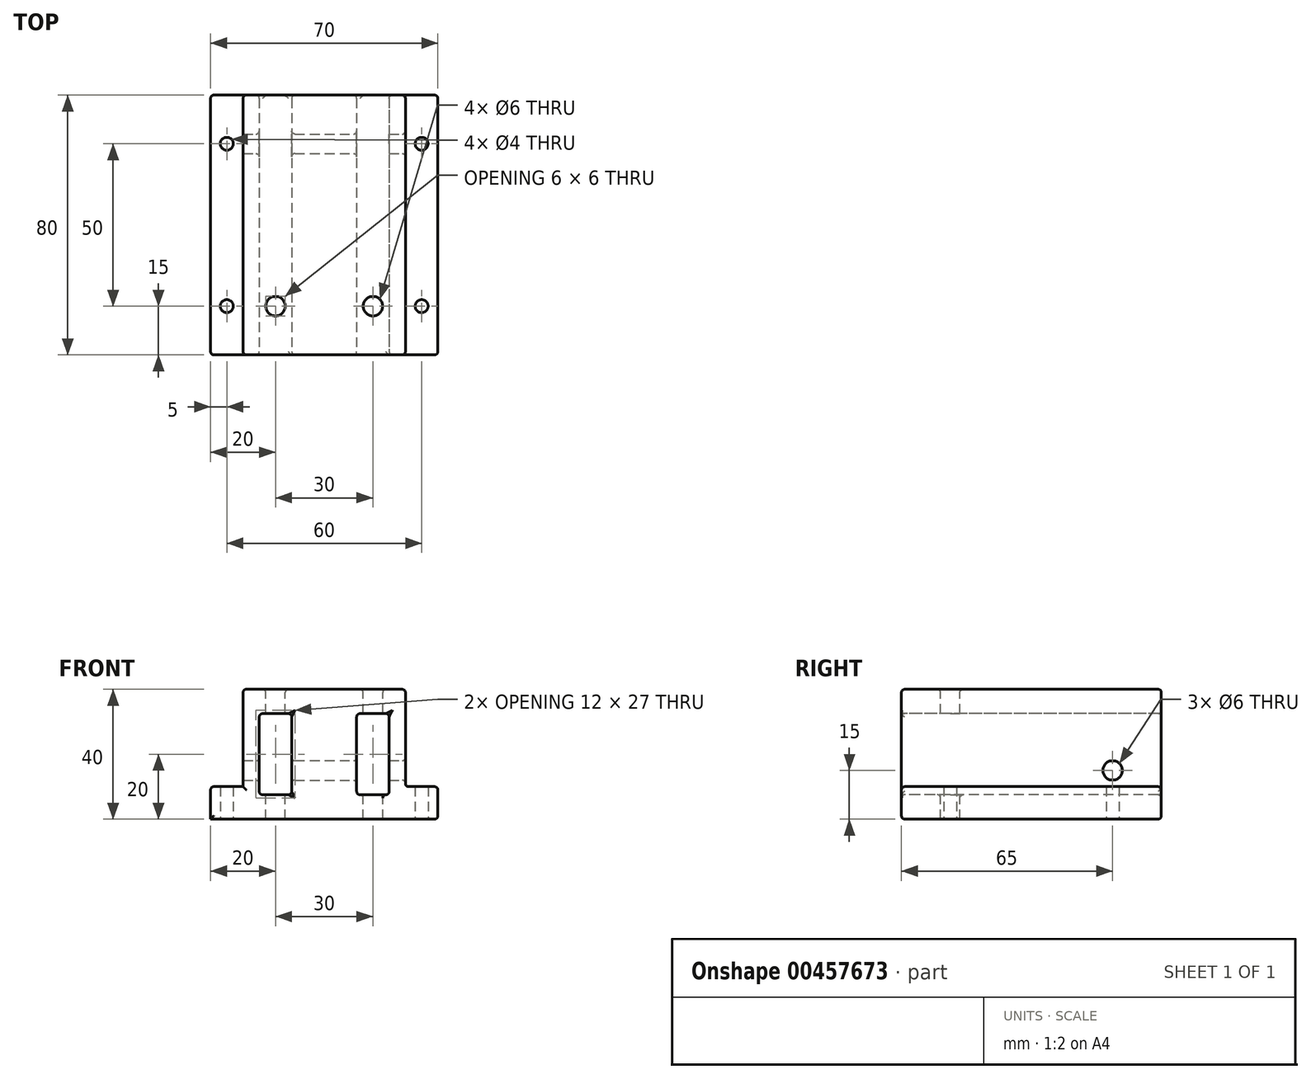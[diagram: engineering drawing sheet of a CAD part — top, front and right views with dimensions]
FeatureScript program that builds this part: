
annotation { "Feature Type Name" : "Feature", "Feature Type Description" : "" }
export const myFeature = defineFeature(function(context is Context, id is Id, definition is map)
    precondition{}
    {
        {
            var Q0;
            Q0=qCreatedBy(makeId("Front.planeOp"),FACE);
            var sketch = newSketch(context, id + "F0", { "sketchPlane" : qUnion([Q0])});
            skLineSegment(sketch, "E0.bottom", {"start": v(-25, 20) * mm, "end": v(25, 20) * mm});
            skLineSegment(sketch, "E0.top", {"start": v(-25, -20) * mm, "end": v(25, -20) * mm});
            skLineSegment(sketch, "E0.left", {"start": v(-25, 20) * mm, "end": v(-25, -20) * mm});
            skLineSegment(sketch, "E0.right", {"start": v(25, 20) * mm, "end": v(25, -20) * mm});
            skPoint(sketch, "E0.middle", {"position": v(0, 0) * mm});
            skSolve(sketch);
        }
        {
            var Q0;
            Q0 = qSketchRegion(id + "F0", true);
            extrude(context, id + "F1", {"entities" : qUnion([Q0]), "depth" : 80 * mm});
        }
        {
            var Q0;
            Q0=makeQuery(id+"F1.opExtrude","CAP_FACE",FACE,{"disambiguationData":[OSD([sQuery(id+"F0.wireOp",EDGE,"E0.bottom"),sQuery(id+"F0.wireOp",EDGE,"E0.top"),sQuery(id+"F0.wireOp",EDGE,"E0.left"),sQuery(id+"F0.wireOp",EDGE,"E0.right")])],"isStart":false});
            var sketch = newSketch(context, id + "F2", { "sketchPlane" : qUnion([Q0])});
            skPoint(sketch, "E1", {"position": v(-15, 0) * mm});
            skPoint(sketch, "E2", {"position": v(15, 0) * mm});
            skLineSegment(sketch, "E3.bottom", {"start": v(-20, 12.5) * mm, "end": v(-10, 12.5) * mm});
            skLineSegment(sketch, "E3.top", {"start": v(-20, -12.5) * mm, "end": v(-10, -12.5) * mm});
            skLineSegment(sketch, "E3.left", {"start": v(-20, 12.5) * mm, "end": v(-20, -12.5) * mm});
            skLineSegment(sketch, "E3.right", {"start": v(-10, 12.5) * mm, "end": v(-10, -12.5) * mm});
            skLineSegment(sketch, "E4.bottom", {"start": v(10, 12.5) * mm, "end": v(20, 12.5) * mm});
            skLineSegment(sketch, "E4.top", {"start": v(10, -12.5) * mm, "end": v(20, -12.5) * mm});
            skLineSegment(sketch, "E4.left", {"start": v(10, 12.5) * mm, "end": v(10, -12.5) * mm});
            skLineSegment(sketch, "E4.right", {"start": v(20, 12.5) * mm, "end": v(20, -12.5) * mm});
            skSolve(sketch);
        }
        {
            var Q0;
            Q0 = qSketchRegion(id + "F2", true);
            extrude(context, id + "F3", {"entities" : qUnion([Q0]), "operationType" : NewBodyOperationType.REMOVE, "endBound" : BoundingType.THROUGH_ALL, "oppositeDirection" : true, "depth" : 25 * mm});
        }
        {
            var Q0;
            Q0=makeQuery(id+"F1.opExtrude","SWEPT_FACE",FACE,{"disambiguationData":[OSD([sQuery(id+"F0.wireOp",EDGE,"E0.right")])]});
            var sketch = newSketch(context, id + "F4", { "sketchPlane" : qUnion([Q0])});
            skPoint(sketch, "E5", {"position": v(-15, -5) * mm});
            skSolve(sketch);
        }
        {
            var Q0;
            Q0=sQuery(id+"F4.wireOp",VERTEX,"E5");
            var Q1;
            Q1=makeQuery(id+"F1.opExtrude","SWEPT_BODY",BODY,{"disambiguationData":[OSD([sQuery(id+"F0.wireOp",EDGE,"E0.bottom"),sQuery(id+"F0.wireOp",EDGE,"E0.top"),sQuery(id+"F0.wireOp",EDGE,"E0.left"),sQuery(id+"F0.wireOp",EDGE,"E0.right")])]});
            hole(context, id + "F5", {"style" : HoleStyle.SIMPLE, "endStyle" : HoleEndStyle.THROUGH, "holeDiameter" : 6 * mm, "isTappedThrough" : true, "tappedDepth" : 12 * mm, "tapClearance" : 3, "startFromSketch" : true, "locations" : qUnion([Q0]), "scope" : qUnion([Q1])});
        }
        {
            var Q0;
            Q0=makeQuery(id+"F1.opExtrude","SWEPT_FACE",FACE,{"disambiguationData":[OSD([sQuery(id+"F0.wireOp",EDGE,"E0.bottom")])]});
            var sketch = newSketch(context, id + "F6", { "sketchPlane" : qUnion([Q0])});
            skPoint(sketch, "E6", {"position": v(-15, -65) * mm});
            skPoint(sketch, "E7", {"position": v(15, -65) * mm});
            skSolve(sketch);
        }
        {
            var Q0;
            Q0=sQuery(id+"F6.wireOp",VERTEX,"E6");
            var Q1;
            Q1=sQuery(id+"F6.wireOp",VERTEX,"E7");
            var Q2;
            Q2=makeQuery(id+"F1.opExtrude","SWEPT_BODY",BODY,{"disambiguationData":[OSD([sQuery(id+"F0.wireOp",EDGE,"E0.bottom"),sQuery(id+"F0.wireOp",EDGE,"E0.top"),sQuery(id+"F0.wireOp",EDGE,"E0.left"),sQuery(id+"F0.wireOp",EDGE,"E0.right")])]});
            hole(context, id + "F7", {"style" : HoleStyle.SIMPLE, "endStyle" : HoleEndStyle.THROUGH, "holeDiameter" : 6 * mm, "isTappedThrough" : true, "tappedDepth" : 12 * mm, "tapClearance" : 3, "startFromSketch" : true, "locations" : qUnion([Q0, Q1]), "scope" : qUnion([Q2])});
        }
        {
            var Q0;
            Q0=makeQuery(id+"F1.opExtrude","SWEPT_FACE",FACE,{"disambiguationData":[OSD([sQuery(id+"F0.wireOp",EDGE,"E0.right")])]});
            var sketch = newSketch(context, id + "F8", { "sketchPlane" : qUnion([Q0])});
            skLineSegment(sketch, "E8", {"start": v(-80, -10) * mm, "end": v(0, -10) * mm});
            skSolve(sketch);
        }
        {
            var Q0;
            {var subQ0=sQuery(id+"F8.wireOp",EDGE,"E8");Q0=makeQuery(id+"F8.imprint","IMPRINT",FACE,{"disambiguationData":[TD([[makeQuery(id+"F8.imprint","IMPRINT",EDGE,{"derivedFrom":subQ0}),-1.0]])]});}
            extrude(context, id + "F9", {"entities" : qUnion([Q0]), "depth" : 10 * mm});
        }
        {
            var Q0;
            Q0=makeQuery(id+"F1.opExtrude","SWEPT_FACE",FACE,{"disambiguationData":[OSD([sQuery(id+"F0.wireOp",EDGE,"E0.left")])]});
            var sketch = newSketch(context, id + "F10", { "sketchPlane" : qUnion([Q0])});
            skLineSegment(sketch, "E9", {"start": v(0, -10) * mm, "end": v(80, -10) * mm});
            skSolve(sketch);
        }
        {
            var Q0;
            {var subQ0=sQuery(id+"F10.wireOp",EDGE,"E9");Q0=makeQuery(id+"F10.imprint","IMPRINT",FACE,{"disambiguationData":[TD([[makeQuery(id+"F10.imprint","IMPRINT",EDGE,{"derivedFrom":subQ0}),-1.0]])]});}
            extrude(context, id + "F11", {"entities" : qUnion([Q0]), "depth" : 10 * mm});
        }
        {
            var Q0;
            Q0=makeQuery(id+"F11.opExtrude","SWEPT_BODY",BODY,{"disambiguationData":[OSD([sQuery(id+"F0.wireOp",EDGE,"E0.top"),sQuery(id+"F0.wireOp",EDGE,"E0.left"),sQuery(id+"F10.wireOp",EDGE,"E9")])]});
            var Q1;
            Q1=makeQuery(id+"F1.opExtrude","SWEPT_BODY",BODY,{"disambiguationData":[OSD([sQuery(id+"F0.wireOp",EDGE,"E0.bottom"),sQuery(id+"F0.wireOp",EDGE,"E0.top"),sQuery(id+"F0.wireOp",EDGE,"E0.left"),sQuery(id+"F0.wireOp",EDGE,"E0.right")])]});
            var Q2;
            Q2=makeQuery(id+"F9.opExtrude","SWEPT_BODY",BODY,{"disambiguationData":[OSD([sQuery(id+"F0.wireOp",EDGE,"E0.top"),sQuery(id+"F0.wireOp",EDGE,"E0.right"),sQuery(id+"F8.wireOp",EDGE,"E8")])]});
            booleanBodies(context, id + "F12", {"operationType" : BooleanOperationType.UNION, "tools" : qUnion([Q0, Q1, Q2])});
        }
        {
            var Q0;
            {var subQ0=sQuery(id+"F0.wireOp",EDGE,"E0.top");Q0=makeQuery(id+"F12.opBoolean","MERGE",FACE,{"derivedFrom":[makeQuery(id+"F1.opExtrude","SWEPT_FACE",FACE,{"disambiguationData":[OSD([subQ0])]}),makeQuery(id+"F9.opExtrude","SWEPT_FACE",FACE,{"disambiguationData":[OSD([subQ0,sQuery(id+"F0.wireOp",EDGE,"E0.right")])]}),makeQuery(id+"F11.opExtrude","SWEPT_FACE",FACE,{"disambiguationData":[OSD([subQ0,sQuery(id+"F0.wireOp",EDGE,"E0.left")])]})]});}
            var sketch = newSketch(context, id + "F13", { "sketchPlane" : qUnion([Q0])});
            skLineSegment(sketch, "E10", {"start": v(-30, 80) * mm, "end": v(-30, 0) * mm});
            skLineSegment(sketch, "E11", {"start": v(30, 80) * mm, "end": v(30, 0) * mm});
            skPoint(sketch, "E12", {"position": v(-30, 65) * mm});
            skPoint(sketch, "E13", {"position": v(30, 65) * mm});
            skPoint(sketch, "E14", {"position": v(-30, 15) * mm});
            skPoint(sketch, "E15", {"position": v(30, 15) * mm});
            skSolve(sketch);
        }
        {
            var Q0;
            Q0=sQuery(id+"F13.wireOp",VERTEX,"E12");
            var Q1;
            Q1=sQuery(id+"F13.wireOp",VERTEX,"E13");
            var Q2;
            Q2=sQuery(id+"F13.wireOp",VERTEX,"E15");
            var Q3;
            Q3=sQuery(id+"F13.wireOp",VERTEX,"E14");
            var Q4;
            Q4=makeQuery(id+"F11.opExtrude","SWEPT_BODY",BODY,{"disambiguationData":[OSD([sQuery(id+"F0.wireOp",EDGE,"E0.top"),sQuery(id+"F0.wireOp",EDGE,"E0.left"),sQuery(id+"F10.wireOp",EDGE,"E9")])]});
            hole(context, id + "F14", {"style" : HoleStyle.SIMPLE, "endStyle" : HoleEndStyle.THROUGH, "holeDiameter" : 4 * mm, "isTappedThrough" : true, "tappedDepth" : 12 * mm, "tapClearance" : 3, "startFromSketch" : true, "locations" : qUnion([Q0, Q1, Q2, Q3]), "scope" : qUnion([Q4])});
        }
        {
            var Q0;
            Q0=makeQuery(id+"F1.opExtrude","SWEPT_FACE",FACE,{"disambiguationData":[OSD([sQuery(id+"F0.wireOp",EDGE,"E0.bottom")])]});
            var Q1;
            Q1=makeQuery(id+"F3.boolean.opBoolean","COPY",FACE,{"derivedFrom":makeQuery(id+"F3.opExtrude","SWEPT_FACE",FACE,{"disambiguationData":[OSD([sQuery(id+"F2.wireOp",EDGE,"E3.left")])]})});
            var Q2;
            {var subQ0=sQuery(id+"F0.wireOp",EDGE,"E0.left");var subQ1=makeQuery(id+"F1.opExtrude","CAP_EDGE",EDGE,{"disambiguationData":[OSD([subQ0])],"isStart":false});var subQ2=sQuery(id+"F0.wireOp",EDGE,"E0.top");var subQ3=sQuery(id+"F0.wireOp",EDGE,"E0.right");var subQ4=makeQuery(id+"F1.opExtrude","CAP_EDGE",EDGE,{"disambiguationData":[OSD([subQ3])],"isStart":false});Q2=makeQuery(id+"F12.opBoolean","MERGE",FACE,{"derivedFrom":[makeQuery(id+"F1.opExtrude","CAP_FACE",FACE,{"disambiguationData":[OSD([sQuery(id+"F0.wireOp",EDGE,"E0.bottom"),subQ2,subQ0,subQ3])],"isStart":false}),makeQuery(id+"F9.opExtrude","SWEPT_FACE",FACE,{"disambiguationData":[OSD([subQ3]),TDD([makeQuery(id+"F8.imprint","IMPRINT",EDGE,{"disambiguationData":[TD([[makeQuery(id+"F8.imprint","INTERSECT",VERTEX,{"derivedFrom":[subQ4,sQuery(id+"F8.wireOp",EDGE,"E8")]}),-1.0]])],"derivedFrom":subQ4})])]}),makeQuery(id+"F11.opExtrude","SWEPT_FACE",FACE,{"disambiguationData":[OSD([subQ0]),TDD([makeQuery(id+"F10.imprint","IMPRINT",EDGE,{"disambiguationData":[TD([[makeQuery(id+"F10.imprint","INTERSECT",VERTEX,{"derivedFrom":[subQ1,sQuery(id+"F10.wireOp",EDGE,"E9")]}),-1.0]])],"derivedFrom":subQ1})])]})]});}
            var Q3;
            Q3=makeQuery(id+"F3.boolean.opBoolean","COPY",FACE,{"derivedFrom":makeQuery(id+"F3.opExtrude","SWEPT_FACE",FACE,{"disambiguationData":[OSD([sQuery(id+"F2.wireOp",EDGE,"E4.left")])]})});
            var Q4;
            Q4=makeQuery(id+"F3.boolean.opBoolean","COPY",FACE,{"derivedFrom":makeQuery(id+"F3.opExtrude","SWEPT_FACE",FACE,{"disambiguationData":[OSD([sQuery(id+"F2.wireOp",EDGE,"E4.top")])]})});
            var Q5;
            Q5=makeQuery(id+"F1.opExtrude","SWEPT_FACE",FACE,{"disambiguationData":[OSD([sQuery(id+"F0.wireOp",EDGE,"E0.right")])]});
            var Q6;
            Q6=makeQuery(id+"F9.opExtrude","CAP_EDGE",EDGE,{"disambiguationData":[OSD([sQuery(id+"F8.wireOp",EDGE,"E8")])],"isStart":false});
            var Q7;
            Q7=makeQuery(id+"F11.opExtrude","CAP_EDGE",EDGE,{"disambiguationData":[OSD([sQuery(id+"F10.wireOp",EDGE,"E9")])],"isStart":false});
            fillet(context, id + "F15", {"entities" : qUnion([Q0, Q1, Q2, Q3, Q4, Q5, Q6, Q7]), "radius" : 1 * mm, "tangentPropagation" : true, "allowEdgeOverflow" : false});
        }
        {
            var Q0;
            {var subQ0=sQuery(id+"F0.wireOp",EDGE,"E0.left");var subQ1=sQuery(id+"F0.wireOp",EDGE,"E0.top");var subQ2=sQuery(id+"F0.wireOp",EDGE,"E0.right");Q0=makeQuery(id+"F12.opBoolean","MERGE",EDGE,{"derivedFrom":[makeQuery(id+"F1.opExtrude","CAP_EDGE",EDGE,{"disambiguationData":[OSD([subQ1])],"isStart":true}),makeQuery(id+"F9.opExtrude","SWEPT_EDGE",EDGE,{"disambiguationData":[OSD([subQ1,subQ2]),TDD([makeQuery(id+"F8.imprint","INTERSECT",VERTEX,{"derivedFrom":[makeQuery(id+"F1.opExtrude","SWEPT_EDGE",EDGE,{"disambiguationData":[OSD([subQ1,subQ2])]}),makeQuery(id+"F1.opExtrude","CAP_EDGE",EDGE,{"disambiguationData":[OSD([subQ2])],"isStart":true})]})])]}),makeQuery(id+"F11.opExtrude","SWEPT_EDGE",EDGE,{"disambiguationData":[OSD([subQ1,subQ0]),TDD([makeQuery(id+"F10.imprint","INTERSECT",VERTEX,{"derivedFrom":[makeQuery(id+"F1.opExtrude","SWEPT_EDGE",EDGE,{"disambiguationData":[OSD([subQ1,subQ0])]}),makeQuery(id+"F1.opExtrude","CAP_EDGE",EDGE,{"disambiguationData":[OSD([subQ0])],"isStart":true})]})])]})]});}
            var Q1;
            Q1=makeQuery(id+"F9.opExtrude","CAP_FACE",FACE,{"disambiguationData":[OSD([sQuery(id+"F0.wireOp",EDGE,"E0.top"),sQuery(id+"F0.wireOp",EDGE,"E0.right"),sQuery(id+"F8.wireOp",EDGE,"E8")])],"isStart":false});
            var Q2;
            Q2=makeQuery(id+"F3.boolean.opBoolean","INTERSECT",EDGE,{"derivedFrom":[makeQuery(id+"F1.opExtrude","CAP_FACE",FACE,{"disambiguationData":[OSD([sQuery(id+"F0.wireOp",EDGE,"E0.bottom"),sQuery(id+"F0.wireOp",EDGE,"E0.top"),sQuery(id+"F0.wireOp",EDGE,"E0.left"),sQuery(id+"F0.wireOp",EDGE,"E0.right")])],"isStart":true}),makeQuery(id+"F3.opExtrude","SWEPT_FACE",FACE,{"disambiguationData":[OSD([sQuery(id+"F2.wireOp",EDGE,"E3.right")])]})]});
            var Q3;
            Q3=makeQuery(id+"F14.hole-2.boolean.opBoolean","INTERSECT",EDGE,{"derivedFrom":[makeQuery(id+"F9.opExtrude","SWEPT_FACE",FACE,{"disambiguationData":[OSD([sQuery(id+"F8.wireOp",EDGE,"E8")])]}),makeQuery(id+"F14.hole-2.opRevolve","SWEPT_FACE",FACE,{"disambiguationData":[OSD([sQuery(id+"F14.hole-2.sketch.wireOp",EDGE,"core_line_2")])]})]});
            var Q4;
            Q4=makeQuery(id+"F14.hole-1.boolean.opBoolean","COPY",FACE,{"derivedFrom":makeQuery(id+"F14.hole-1.opRevolve","SWEPT_FACE",FACE,{"disambiguationData":[OSD([sQuery(id+"F14.hole-1.sketch.wireOp",EDGE,"core_line_2")])]})});
            var Q5;
            Q5=makeQuery(id+"F14.hole-2.boolean.opBoolean","COPY",FACE,{"derivedFrom":makeQuery(id+"F14.hole-2.opRevolve","SWEPT_FACE",FACE,{"disambiguationData":[OSD([sQuery(id+"F14.hole-2.sketch.wireOp",EDGE,"core_line_2")])]})});
            var Q6;
            Q6=makeQuery(id+"F14.hole-3.boolean.opBoolean","COPY",FACE,{"derivedFrom":makeQuery(id+"F14.hole-3.opRevolve","SWEPT_FACE",FACE,{"disambiguationData":[OSD([sQuery(id+"F14.hole-3.sketch.wireOp",EDGE,"core_line_2")])]})});
            var Q7;
            Q7=makeQuery(id+"F14.hole-0.boolean.opBoolean","COPY",FACE,{"derivedFrom":makeQuery(id+"F14.hole-0.opRevolve","SWEPT_FACE",FACE,{"disambiguationData":[OSD([sQuery(id+"F14.hole-0.sketch.wireOp",EDGE,"core_line_2")])]})});
            var Q8;
            Q8=makeQuery(id+"F3.boolean.opBoolean","COPY",EDGE,{"derivedFrom":makeQuery(id+"F3.opExtrude","SWEPT_EDGE",EDGE,{"disambiguationData":[OSD([sQuery(id+"F2.wireOp",EDGE,"E3.top"),sQuery(id+"F2.wireOp",EDGE,"E3.right")])]})});
            var Q9;
            Q9=makeQuery(id+"F3.boolean.opBoolean","COPY",FACE,{"derivedFrom":makeQuery(id+"F3.opExtrude","SWEPT_FACE",FACE,{"disambiguationData":[OSD([sQuery(id+"F2.wireOp",EDGE,"E3.right")])]})});
            var Q10;
            Q10=makeQuery(id+"F3.boolean.opBoolean","COPY",EDGE,{"derivedFrom":makeQuery(id+"F3.opExtrude","SWEPT_EDGE",EDGE,{"disambiguationData":[OSD([sQuery(id+"F2.wireOp",EDGE,"E4.bottom"),sQuery(id+"F2.wireOp",EDGE,"E4.right")])]})});
            var Q11;
            {var subQ0=makeQuery(id+"F3.boolean.opBoolean","COPY",FACE,{"derivedFrom":makeQuery(id+"F3.opExtrude","SWEPT_FACE",FACE,{"disambiguationData":[OSD([sQuery(id+"F2.wireOp",EDGE,"E3.left")])]})});var subQ1=makeQuery(id+"F5.hole-0.opRevolve","SWEPT_FACE",FACE,{"disambiguationData":[OSD([sQuery(id+"F5.hole-0.sketch.wireOp",EDGE,"core_line_2")])]});Q11=makeQuery(id+"F15.opFillet","BLEND_EDGE",EDGE,{"blendedFrom":[makeQuery(id+"F5.hole-0.boolean.opBoolean","INTERSECT",EDGE,{"derivedFrom":[subQ0,subQ1]}),makeQuery(id+"F5.hole-0.boolean.opBoolean","COPY",FACE,{"disambiguationData":[TD([makeQuery(id+"F1.opExtrude","SWEPT_FACE",FACE,{"disambiguationData":[OSD([sQuery(id+"F0.wireOp",EDGE,"E0.left")])]})])],"derivedFrom":subQ1})],"blendedInto":[makeQuery(id+"F5.hole-0.boolean.opBoolean","COPY",FACE,{"disambiguationData":[TD([makeQuery(id+"F1.opExtrude","SWEPT_FACE",FACE,{"disambiguationData":[OSD([sQuery(id+"F0.wireOp",EDGE,"E0.left")])]})])],"derivedFrom":subQ1})]});}
            var Q12;
            Q12=makeQuery(id+"F5.hole-0.boolean.opBoolean","INTERSECT",EDGE,{"derivedFrom":[makeQuery(id+"F1.opExtrude","SWEPT_FACE",FACE,{"disambiguationData":[OSD([sQuery(id+"F0.wireOp",EDGE,"E0.left")])]}),makeQuery(id+"F5.hole-0.opRevolve","SWEPT_FACE",FACE,{"disambiguationData":[OSD([sQuery(id+"F5.hole-0.sketch.wireOp",EDGE,"core_line_2")])]})]});
            var Q13;
            Q13=makeQuery(id+"F5.hole-0.boolean.opBoolean","INTERSECT",EDGE,{"derivedFrom":[makeQuery(id+"F3.boolean.opBoolean","COPY",FACE,{"derivedFrom":makeQuery(id+"F3.opExtrude","SWEPT_FACE",FACE,{"disambiguationData":[OSD([sQuery(id+"F2.wireOp",EDGE,"E4.right")])]})}),makeQuery(id+"F5.hole-0.opRevolve","SWEPT_FACE",FACE,{"disambiguationData":[OSD([sQuery(id+"F5.hole-0.sketch.wireOp",EDGE,"core_line_2")])]})]});
            var Q14;
            {var subQ0=makeQuery(id+"F3.boolean.opBoolean","COPY",FACE,{"derivedFrom":makeQuery(id+"F3.opExtrude","SWEPT_FACE",FACE,{"disambiguationData":[OSD([sQuery(id+"F2.wireOp",EDGE,"E4.top")])]})});var subQ1=makeQuery(id+"F7.hole-1.opRevolve","SWEPT_FACE",FACE,{"disambiguationData":[OSD([sQuery(id+"F7.hole-1.sketch.wireOp",EDGE,"core_line_2")])]});Q14=makeQuery(id+"F15.opFillet","BLEND_EDGE",EDGE,{"blendedFrom":[makeQuery(id+"F7.hole-1.boolean.opBoolean","INTERSECT",EDGE,{"derivedFrom":[subQ0,subQ1]}),makeQuery(id+"F7.hole-1.boolean.opBoolean","COPY",FACE,{"disambiguationData":[TD([makeQuery(id+"F1.opExtrude","SWEPT_FACE",FACE,{"disambiguationData":[OSD([sQuery(id+"F0.wireOp",EDGE,"E0.top")])]})])],"derivedFrom":subQ1})],"blendedInto":[makeQuery(id+"F7.hole-1.boolean.opBoolean","COPY",FACE,{"disambiguationData":[TD([makeQuery(id+"F1.opExtrude","SWEPT_FACE",FACE,{"disambiguationData":[OSD([sQuery(id+"F0.wireOp",EDGE,"E0.top")])]})])],"derivedFrom":subQ1})]});}
            var Q15;
            Q15=makeQuery(id+"F7.hole-0.boolean.opBoolean","INTERSECT",EDGE,{"derivedFrom":[makeQuery(id+"F1.opExtrude","SWEPT_FACE",FACE,{"disambiguationData":[OSD([sQuery(id+"F0.wireOp",EDGE,"E0.top")])]}),makeQuery(id+"F7.hole-0.opRevolve","SWEPT_FACE",FACE,{"disambiguationData":[OSD([sQuery(id+"F7.hole-0.sketch.wireOp",EDGE,"core_line_2")])]})]});
            var Q16;
            Q16=makeQuery(id+"F7.hole-1.boolean.opBoolean","INTERSECT",EDGE,{"derivedFrom":[makeQuery(id+"F1.opExtrude","SWEPT_FACE",FACE,{"disambiguationData":[OSD([sQuery(id+"F0.wireOp",EDGE,"E0.top")])]}),makeQuery(id+"F7.hole-1.opRevolve","SWEPT_FACE",FACE,{"disambiguationData":[OSD([sQuery(id+"F7.hole-1.sketch.wireOp",EDGE,"core_line_2")])]})]});
            var Q17;
            Q17=makeQuery(id+"F7.hole-0.boolean.opBoolean","INTERSECT",EDGE,{"derivedFrom":[makeQuery(id+"F3.boolean.opBoolean","COPY",FACE,{"derivedFrom":makeQuery(id+"F3.opExtrude","SWEPT_FACE",FACE,{"disambiguationData":[OSD([sQuery(id+"F2.wireOp",EDGE,"E3.top")])]})}),makeQuery(id+"F7.hole-0.opRevolve","SWEPT_FACE",FACE,{"disambiguationData":[OSD([sQuery(id+"F7.hole-0.sketch.wireOp",EDGE,"core_line_2")])]})]});
            var Q18;
            Q18=makeQuery(id+"F7.hole-1.boolean.opBoolean","INTERSECT",EDGE,{"derivedFrom":[makeQuery(id+"F3.boolean.opBoolean","COPY",FACE,{"derivedFrom":makeQuery(id+"F3.opExtrude","SWEPT_FACE",FACE,{"disambiguationData":[OSD([sQuery(id+"F2.wireOp",EDGE,"E4.bottom")])]})}),makeQuery(id+"F7.hole-1.opRevolve","SWEPT_FACE",FACE,{"disambiguationData":[OSD([sQuery(id+"F7.hole-1.sketch.wireOp",EDGE,"core_line_2")])]})]});
            var Q19;
            Q19=makeQuery(id+"F7.hole-0.boolean.opBoolean","INTERSECT",EDGE,{"derivedFrom":[makeQuery(id+"F3.boolean.opBoolean","COPY",FACE,{"derivedFrom":makeQuery(id+"F3.opExtrude","SWEPT_FACE",FACE,{"disambiguationData":[OSD([sQuery(id+"F2.wireOp",EDGE,"E3.bottom")])]})}),makeQuery(id+"F7.hole-0.opRevolve","SWEPT_FACE",FACE,{"disambiguationData":[OSD([sQuery(id+"F7.hole-0.sketch.wireOp",EDGE,"core_line_2")])]})]});
            var Q20;
            Q20=makeQuery(id+"F1.opExtrude","CAP_EDGE",EDGE,{"disambiguationData":[OSD([sQuery(id+"F0.wireOp",EDGE,"E0.left")])],"isStart":true});
            var Q21;
            {var subQ0=sQuery(id+"F10.wireOp",EDGE,"E9");var subQ1=sQuery(id+"F0.wireOp",EDGE,"E0.left");Q21=makeQuery(id+"F11.opExtrude","SWEPT_EDGE",EDGE,{"disambiguationData":[OSD([subQ1,subQ0]),TDD([makeQuery(id+"F10.imprint","INTERSECT",VERTEX,{"derivedFrom":[makeQuery(id+"F1.opExtrude","CAP_EDGE",EDGE,{"disambiguationData":[OSD([subQ1])],"isStart":true}),subQ0]})])]});}
            var Q22;
            {var subQ0=sQuery(id+"F0.wireOp",EDGE,"E0.left");var subQ1=makeQuery(id+"F1.opExtrude","CAP_EDGE",EDGE,{"disambiguationData":[OSD([subQ0])],"isStart":true});var subQ2=sQuery(id+"F0.wireOp",EDGE,"E0.top");var subQ3=sQuery(id+"F10.wireOp",EDGE,"E9");var subQ4=sQuery(id+"F0.wireOp",EDGE,"E0.right");var subQ5=makeQuery(id+"F1.opExtrude","CAP_EDGE",EDGE,{"disambiguationData":[OSD([subQ4])],"isStart":true});Q22=makeQuery(id+"F15.opFillet","BLEND_EDGE",EDGE,{"blendedFrom":[makeQuery(id+"F11.opExtrude","CAP_EDGE",EDGE,{"disambiguationData":[OSD([subQ3])],"isStart":false}),makeQuery(id+"F12.opBoolean","MERGE",FACE,{"derivedFrom":[makeQuery(id+"F1.opExtrude","CAP_FACE",FACE,{"disambiguationData":[OSD([sQuery(id+"F0.wireOp",EDGE,"E0.bottom"),subQ2,subQ0,subQ4])],"isStart":true}),makeQuery(id+"F9.opExtrude","SWEPT_FACE",FACE,{"disambiguationData":[OSD([subQ4]),TDD([makeQuery(id+"F8.imprint","IMPRINT",EDGE,{"disambiguationData":[TD([[makeQuery(id+"F8.imprint","INTERSECT",VERTEX,{"derivedFrom":[subQ5,sQuery(id+"F8.wireOp",EDGE,"E8")]}),-1.0]])],"derivedFrom":subQ5})])]}),makeQuery(id+"F11.opExtrude","SWEPT_FACE",FACE,{"disambiguationData":[OSD([subQ0]),TDD([makeQuery(id+"F10.imprint","IMPRINT",EDGE,{"disambiguationData":[TD([[makeQuery(id+"F10.imprint","INTERSECT",VERTEX,{"derivedFrom":[subQ1,subQ3]}),-1.0]])],"derivedFrom":subQ1})])]})]})],"blendedInto":[makeQuery(id+"F12.opBoolean","MERGE",FACE,{"derivedFrom":[makeQuery(id+"F1.opExtrude","CAP_FACE",FACE,{"disambiguationData":[OSD([sQuery(id+"F0.wireOp",EDGE,"E0.bottom"),subQ2,subQ0,subQ4])],"isStart":true}),makeQuery(id+"F9.opExtrude","SWEPT_FACE",FACE,{"disambiguationData":[OSD([subQ4]),TDD([makeQuery(id+"F8.imprint","IMPRINT",EDGE,{"disambiguationData":[TD([[makeQuery(id+"F8.imprint","INTERSECT",VERTEX,{"derivedFrom":[subQ5,sQuery(id+"F8.wireOp",EDGE,"E8")]}),-1.0]])],"derivedFrom":subQ5})])]}),makeQuery(id+"F11.opExtrude","SWEPT_FACE",FACE,{"disambiguationData":[OSD([subQ0]),TDD([makeQuery(id+"F10.imprint","IMPRINT",EDGE,{"disambiguationData":[TD([[makeQuery(id+"F10.imprint","INTERSECT",VERTEX,{"derivedFrom":[subQ1,subQ3]}),-1.0]])],"derivedFrom":subQ1})])]})]})]});}
            fillet(context, id + "F16", {"entities" : qUnion([Q0, Q1, Q2, Q3, Q4, Q5, Q6, Q7, Q8, Q9, Q10, Q11, Q12, Q13, Q14, Q15, Q16, Q17, Q18, Q19, Q20, Q21, Q22]), "radius" : 1 * mm, "tangentPropagation" : true, "allowEdgeOverflow" : false});
        }
    });
